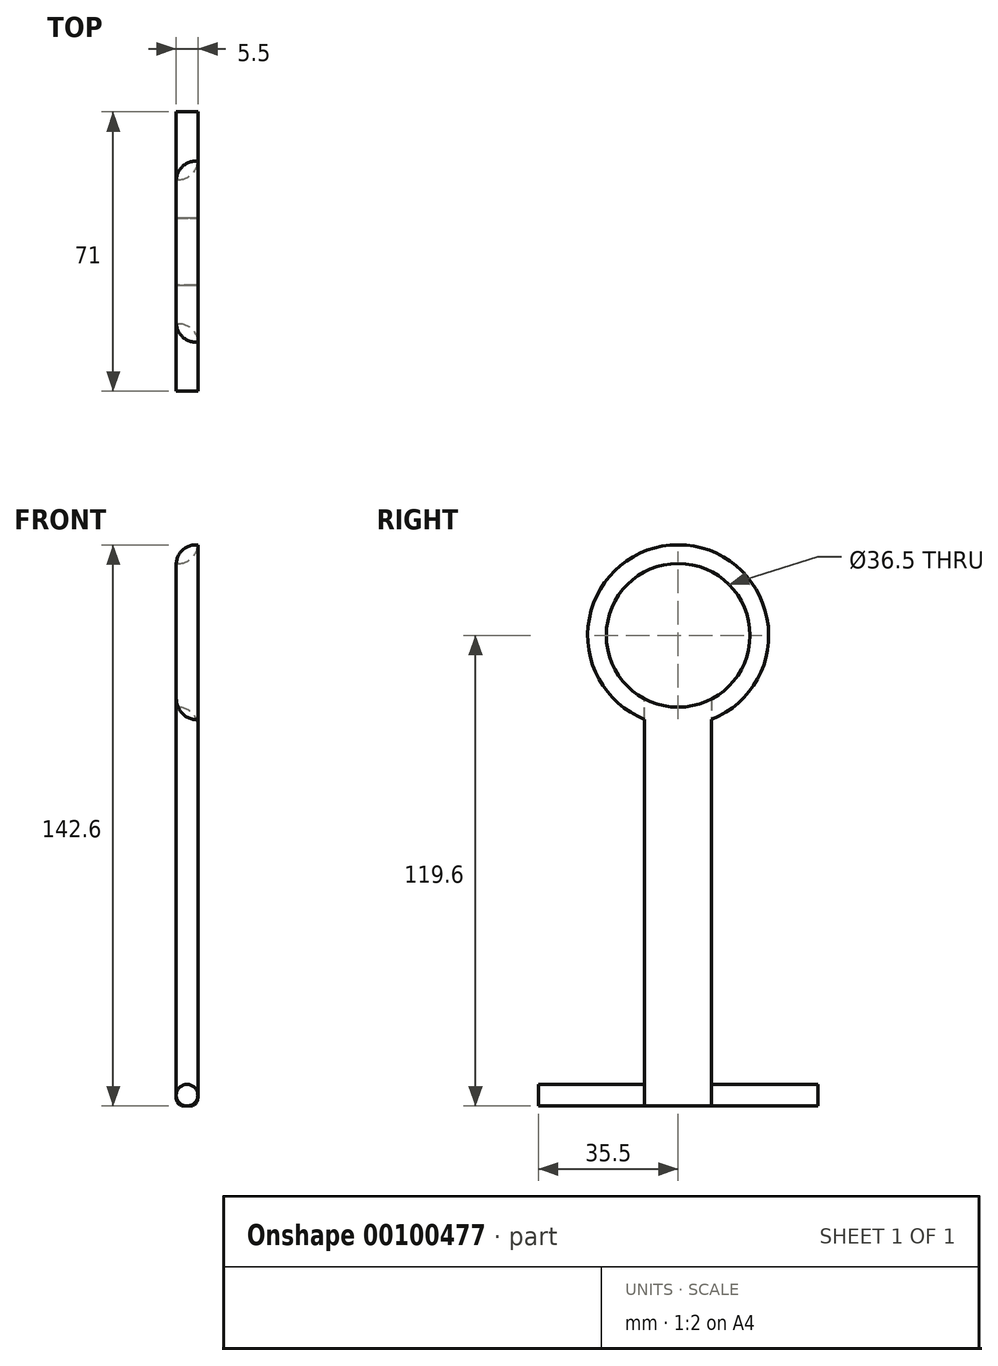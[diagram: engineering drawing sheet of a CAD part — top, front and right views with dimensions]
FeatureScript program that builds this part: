
annotation { "Feature Type Name" : "Feature", "Feature Type Description" : "" }
export const myFeature = defineFeature(function(context is Context, id is Id, definition is map)
    precondition{}
    {
        {
            var Q0;
            Q0=qCreatedBy(makeId("Right.planeOp"),FACE);
            var sketch = newSketch(context, id + "F0", { "sketchPlane" : qUnion([Q0])});
            skLineSegment(sketch, "E0", {"start": v(-10, 0) * mm, "end": v(-10, 100) * mm});
            skLineSegment(sketch, "E1", {"start": v(-10, 0) * mm, "end": v(7, 0) * mm});
            skLineSegment(sketch, "E2", {"start": v(7, 0) * mm, "end": v(7, 100) * mm});
            skLineSegment(sketch, "E3", {"start": v(7, 100) * mm, "end": v(-10, 100) * mm});
            skSolve(sketch);
        }
        {
            var Q0;
            Q0 = qSketchRegion(id + "F0", true);
            extrude(context, id + "F1", {"entities" : qUnion([Q0]), "endBound" : BoundingType.SYMMETRIC, "depth" : 5.5 * mm});
        }
        {
            var Q0;
            Q0=makeQuery(id+"F1.opExtrude","SWEPT_FACE",FACE,{"disambiguationData":[OSD([sQuery(id+"F0.wireOp",EDGE,"E0")])]});
            var sketch = newSketch(context, id + "F2", { "sketchPlane" : qUnion([Q0])});
            skCircle(sketch, "E4", {"center": v(0, 2.75) * mm, "radius": 2.75 * mm});
            skLineSegment(sketch, "E5", {"start": v(0, 5.5) * mm, "end": v(0, 2.75) * mm});
            skLineSegment(sketch, "E6", {"start": v(0, 0) * mm, "end": v(0, 2.75) * mm});
            skLineSegment(sketch, "E7", {"start": v(0, 100) * mm, "end": v(0, 2.75) * mm});
            skSolve(sketch);
        }
        {
            var Q0;
            Q0=makeQuery(id+"F2.imprint","IMPRINT",FACE,{"disambiguationData":[TD([[makeQuery(id+"F2.imprint","IMPRINT",EDGE,{"derivedFrom":sQuery(id+"F2.wireOp",EDGE,"E4")}),1.0]])]});
            extrude(context, id + "F3", {"entities" : qUnion([Q0]), "operationType" : NewBodyOperationType.ADD, "depth" : 27 * mm});
        }
        {
            var Q0;
            Q0=makeQuery(id+"F1.opExtrude","SWEPT_FACE",FACE,{"disambiguationData":[OSD([sQuery(id+"F0.wireOp",EDGE,"E2")])]});
            var sketch = newSketch(context, id + "F4", { "sketchPlane" : qUnion([Q0])});
            skLineSegment(sketch, "E8", {"start": v(0, 100) * mm, "end": v(0, 2.75) * mm});
            skCircle(sketch, "E9", {"center": v(0, 2.75) * mm, "radius": 2.75 * mm});
            skPoint(sketch, "E10", {"position": v(0, 0) * mm});
            skSolve(sketch);
        }
        {
            var Q0;
            Q0 = qSketchRegion(id + "F4", true);
            extrude(context, id + "F5", {"entities" : qUnion([Q0]), "operationType" : NewBodyOperationType.ADD, "depth" : 27 * mm});
        }
        {
            var Q0;
            Q0=makeQuery(id+"F1.opExtrude","CAP_FACE",FACE,{"disambiguationData":[OSD([sQuery(id+"F0.wireOp",EDGE,"E0"),sQuery(id+"F0.wireOp",EDGE,"E1"),sQuery(id+"F0.wireOp",EDGE,"E2"),sQuery(id+"F0.wireOp",EDGE,"E3")])],"isStart":false});
            var sketch = newSketch(context, id + "F6", { "sketchPlane" : qUnion([Q0])});
            skCircle(sketch, "E11", {"center": v(-1.5, 119.6) * mm, "radius": 18.25 * mm});
            skCircle(sketch, "E12", {"center": v(-1.5, 119.6) * mm, "radius": 23 * mm});
            skLineSegment(sketch, "E13", {"start": v(-1.5, 100) * mm, "end": v(-1.5, 119.6) * mm});
            skSolve(sketch);
        }
        {
            var Q0;
            {var subQ0=sQuery(id+"F6.wireOp",EDGE,"E11");var subQ1=makeQuery(id+"F1.opExtrude","CAP_EDGE",EDGE,{"disambiguationData":[OSD([sQuery(id+"F0.wireOp",EDGE,"E0")])],"isStart":false});var subQ2=makeQuery(id+"F6.imprint","INTERSECT",VERTEX,{"derivedFrom":[subQ1,subQ0]});Q0=makeQuery(id+"F6.imprint","IMPRINT",FACE,{"disambiguationData":[TD([[makeQuery(id+"F6.imprint","IMPRINT",EDGE,{"disambiguationData":[TD([[subQ2,1.0]])],"derivedFrom":subQ0}),-1.0]])]});}
            extrude(context, id + "F7", {"entities" : qUnion([Q0]), "operationType" : NewBodyOperationType.ADD, "oppositeDirection" : true, "depth" : 5.5 * mm});
        }
        {
            var Q0;
            Q0=makeQuery(id+"F7.opExtrude","CAP_EDGE",EDGE,{"disambiguationData":[OSD([sQuery(id+"F6.wireOp",EDGE,"E11")])],"isStart":true});
            var Q1;
            Q1=makeQuery(id+"F7.opExtrude","CAP_EDGE",EDGE,{"disambiguationData":[OSD([sQuery(id+"F6.wireOp",EDGE,"E12")])],"isStart":false});
            fillet(context, id + "F8", {"entities" : qUnion([Q0, Q1]), "radius" : 5 * mm, "tangentPropagation" : true, "allowEdgeOverflow" : false});
        }
        {
            var Q0;
            Q0=makeQuery(id+"F1.opExtrude","CAP_EDGE",EDGE,{"disambiguationData":[OSD([sQuery(id+"F0.wireOp",EDGE,"E1")])],"isStart":false});
            var Q1;
            Q1=makeQuery(id+"F1.opExtrude","CAP_EDGE",EDGE,{"disambiguationData":[OSD([sQuery(id+"F0.wireOp",EDGE,"E1")])],"isStart":true});
            fillet(context, id + "F9", {"entities" : qUnion([Q0, Q1]), "radius" : 2 * mm, "tangentPropagation" : true, "allowEdgeOverflow" : false});
        }
    });
